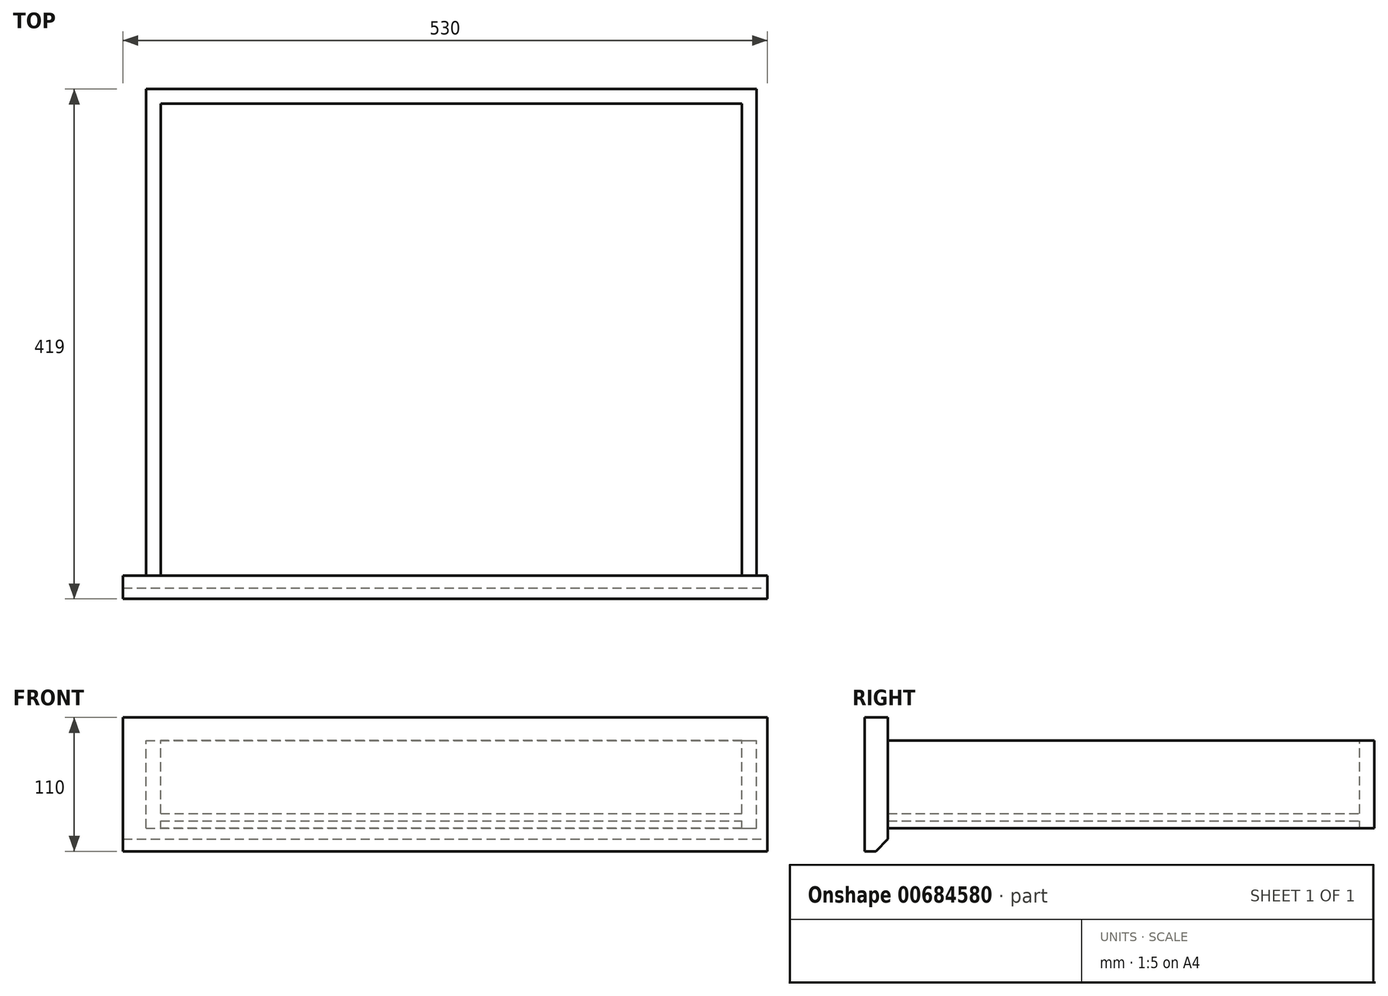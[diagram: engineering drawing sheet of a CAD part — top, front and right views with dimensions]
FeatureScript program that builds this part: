
annotation { "Feature Type Name" : "Feature", "Feature Type Description" : "" }
export const myFeature = defineFeature(function(context is Context, id is Id, definition is map)
    precondition{}
    {
        {
            var Q0;
            Q0=qCreatedBy(makeId("Top.planeOp"),FACE);
            var sketch = newSketch(context, id + "F0", { "sketchPlane" : qUnion([Q0])});
            skLineSegment(sketch, "E0.top", {"start": v(0, 400) * mm, "end": v(-502, 400) * mm});
            skLineSegment(sketch, "E0.left", {"start": v(0, 0) * mm, "end": v(0, 400) * mm});
            skLineSegment(sketch, "E0.right", {"start": v(-502, 0) * mm, "end": v(-502, 400) * mm});
            skLineSegment(sketch, "E1.0", {"start": v(-12, 0) * mm, "end": v(-12, 388) * mm});
            skLineSegment(sketch, "E1.1", {"start": v(-12, 388) * mm, "end": v(-490, 388) * mm});
            skLineSegment(sketch, "E1.2", {"start": v(-490, 0) * mm, "end": v(-490, 388) * mm});
            skLineSegment(sketch, "E2", {"start": v(0, 0) * mm, "end": v(9, 0) * mm});
            skLineSegment(sketch, "E3", {"start": v(9, 0) * mm, "end": v(9, -19) * mm});
            skLineSegment(sketch, "E4", {"start": v(-502, 0) * mm, "end": v(-521, 0) * mm});
            skLineSegment(sketch, "E5", {"start": v(9, -19) * mm, "end": v(-521, -19) * mm});
            skLineSegment(sketch, "E6", {"start": v(-521, -19) * mm, "end": v(-521, 0) * mm});
            skLineSegment(sketch, "E7", {"start": v(-12, 0) * mm, "end": v(-490, 0) * mm});
            skSolve(sketch);
        }
        {
            var Q0;
            Q0 = qSketchRegion(id + "F0", true);
            extrude(context, id + "F1", {"entities" : qUnion([Q0]), "oppositeDirection" : true, "depth" : 110 * mm, "offsetDistance" : 25 * mm});
        }
        {
            var Q0;
            Q0=qCreatedBy(makeId("Right.planeOp"),FACE);
            var sketch = newSketch(context, id + "F2", { "sketchPlane" : qUnion([Q0])});
            skLineSegment(sketch, "E8", {"start": v(0, 0) * mm, "end": v(0, -110) * mm, "construction": true});
            skLineSegment(sketch, "E9", {"start": v(0, -110) * mm, "end": v(0, -91) * mm});
            skLineSegment(sketch, "E10", {"start": v(0, -91) * mm, "end": v(400, -91) * mm});
            skLineSegment(sketch, "E11", {"start": v(400, -91) * mm, "end": v(400, -110) * mm});
            skLineSegment(sketch, "E12", {"start": v(400, -110) * mm, "end": v(0, -110) * mm});
            skLineSegment(sketch, "E13.bottom", {"start": v(0, 0) * mm, "end": v(400, 0) * mm});
            skLineSegment(sketch, "E13.top", {"start": v(0, -19) * mm, "end": v(400, -19) * mm});
            skLineSegment(sketch, "E13.left", {"start": v(0, 0) * mm, "end": v(0, -19) * mm});
            skLineSegment(sketch, "E13.right", {"start": v(400, 0) * mm, "end": v(400, -19) * mm});
            skSolve(sketch);
        }
        {
            var Q0;
            Q0 = qSketchRegion(id + "F2", true);
            extrude(context, id + "F3", {"entities" : qUnion([Q0]), "operationType" : NewBodyOperationType.REMOVE, "oppositeDirection" : true, "depth" : 502 * mm, "offsetDistance" : 25 * mm});
        }
        {
            var Q0;
            Q0=qCreatedBy(makeId("Right.planeOp"),FACE);
            var sketch = newSketch(context, id + "F4", { "sketchPlane" : qUnion([Q0])});
            skLineSegment(sketch, "E14", {"start": v(0, 0) * mm, "end": v(0, -108.89) * mm, "construction": true});
            skLineSegment(sketch, "E15", {"start": v(0, -108.89) * mm, "end": v(0, -89.89) * mm, "construction": true});
            skLineSegment(sketch, "E16", {"start": v(0, -89.89) * mm, "end": v(0, -84.89) * mm, "construction": true});
            skLineSegment(sketch, "E17", {"start": v(0, -84.89) * mm, "end": v(0, -80.56) * mm, "construction": true});
            skLineSegment(sketch, "E18.bottom", {"start": v(0, -84.89) * mm, "end": v(400, -84.89) * mm});
            skLineSegment(sketch, "E18.top", {"start": v(0, -78.89) * mm, "end": v(400, -78.89) * mm});
            skLineSegment(sketch, "E18.left", {"start": v(0, -84.89) * mm, "end": v(0, -78.89) * mm});
            skLineSegment(sketch, "E18.right", {"start": v(400, -84.89) * mm, "end": v(400, -78.89) * mm});
            skSolve(sketch);
        }
        {
            var Q0;
            Q0 = qSketchRegion(id + "F4", true);
            extrude(context, id + "F5", {"entities" : qUnion([Q0]), "operationType" : NewBodyOperationType.ADD, "oppositeDirection" : true, "depth" : 502 * mm, "offsetDistance" : 25 * mm});
        }
        {
            var Q0;
            Q0=qCreatedBy(makeId("Right.planeOp"),FACE);
            var sketch = newSketch(context, id + "F6", { "sketchPlane" : qUnion([Q0])});
            skLineSegment(sketch, "E19", {"start": v(0, 0) * mm, "end": v(0, -110) * mm, "construction": true});
            skLineSegment(sketch, "E20", {"start": v(0, -110) * mm, "end": v(-10, -110) * mm});
            skLineSegment(sketch, "E21", {"start": v(-10, -110) * mm, "end": v(0, -100) * mm});
            skLineSegment(sketch, "E22", {"start": v(0, -100) * mm, "end": v(0, -110) * mm});
            skSolve(sketch);
        }
        {
            var Q0;
            Q0 = qSketchRegion(id + "F6", true);
            extrude(context, id + "F7", {"entities" : qUnion([Q0]), "operationType" : NewBodyOperationType.REMOVE, "endBound" : BoundingType.SYMMETRIC, "oppositeDirection" : true, "depth" : 1118 * mm, "offsetDistance" : 25 * mm});
        }
    });
